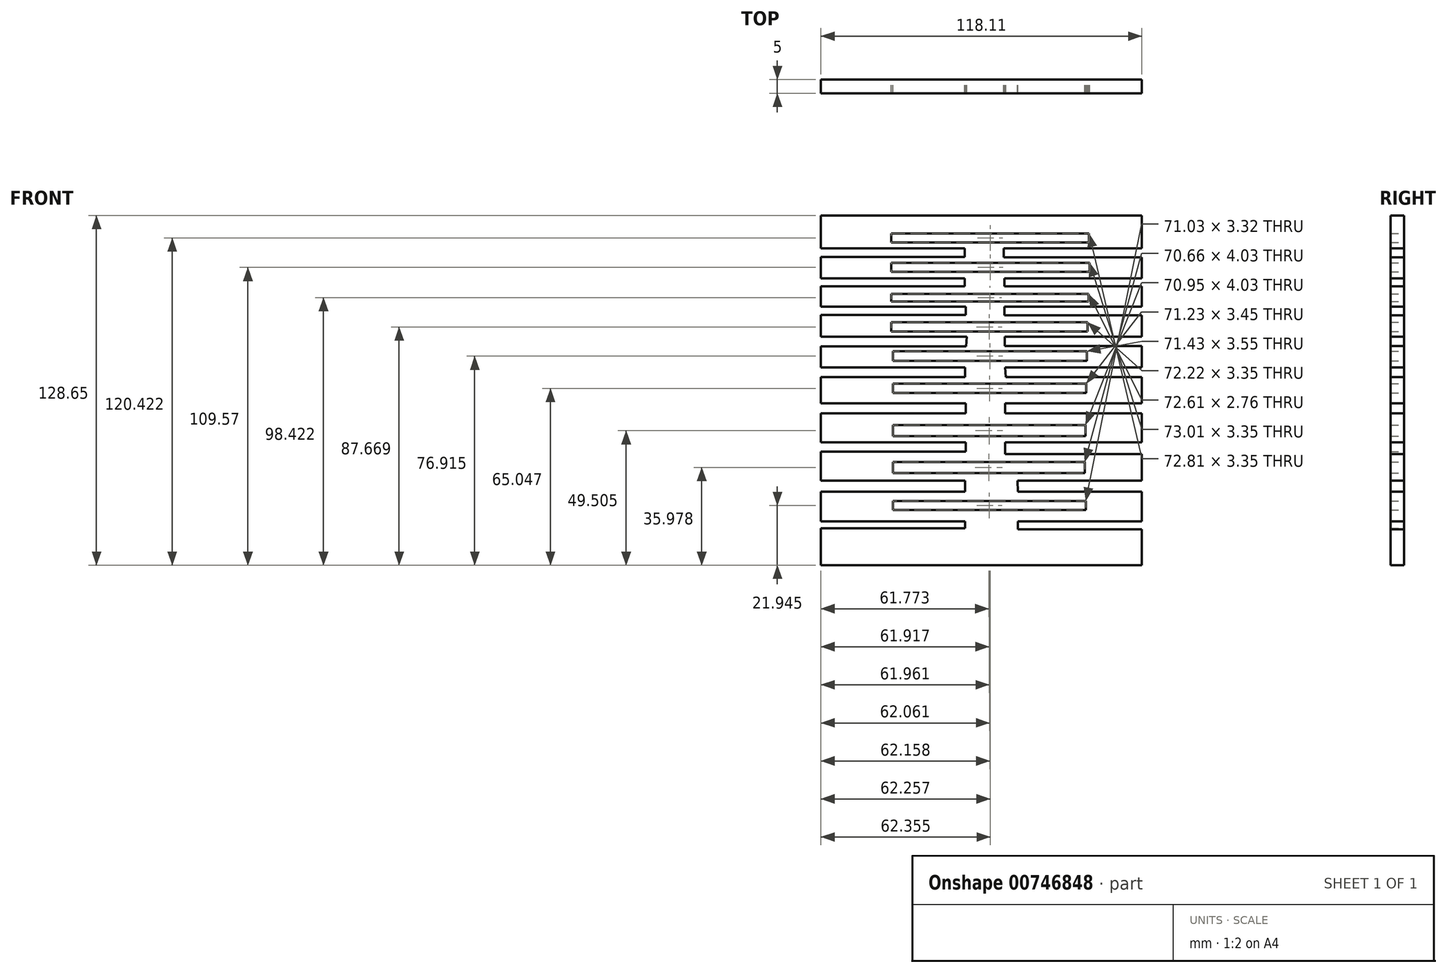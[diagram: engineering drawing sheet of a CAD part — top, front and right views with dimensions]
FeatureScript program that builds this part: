
annotation { "Feature Type Name" : "Feature", "Feature Type Description" : "" }
export const myFeature = defineFeature(function(context is Context, id is Id, definition is map)
    precondition{}
    {
        {
            var Q0;
            Q0=qCreatedBy(makeId("Front.planeOp"),FACE);
            var sketch = newSketch(context, id + "F0", { "sketchPlane" : qUnion([Q0])});
            skLineSegment(sketch, "E0.bottom", {"start": v(-61.27, 59.43) * mm, "end": v(56.84, 59.43) * mm});
            skLineSegment(sketch, "E0.top", {"start": v(-61.27, -69.22) * mm, "end": v(56.84, -69.22) * mm});
            skLineSegment(sketch, "E0.left", {"start": v(-61.27, 59.43) * mm, "end": v(-61.27, 47.35) * mm});
            skLineSegment(sketch, "E0.right", {"start": v(56.84, 59.43) * mm, "end": v(56.84, 47.35) * mm});
            skLineSegment(sketch, "E1.bottom", {"start": v(-34.83, -45.62) * mm, "end": v(36.2, -45.62) * mm});
            skLineSegment(sketch, "E1.top", {"start": v(-34.83, -48.93) * mm, "end": v(36.2, -48.93) * mm});
            skLineSegment(sketch, "E1.left", {"start": v(-34.83, -45.62) * mm, "end": v(-34.83, -48.93) * mm});
            skLineSegment(sketch, "E1.right", {"start": v(36.2, -45.62) * mm, "end": v(36.2, -48.93) * mm});
            skLineSegment(sketch, "E2.bottom", {"start": v(56.84, -38.13) * mm, "end": v(11.08, -38.13) * mm});
            skLineSegment(sketch, "E2.top", {"start": v(56.84, -42.16) * mm, "end": v(11.2, -42.16) * mm});
            skLineSegment(sketch, "E2.right", {"start": v(11.08, -38.13) * mm, "end": v(11.2, -42.16) * mm});
            skLineSegment(sketch, "E3.bottom", {"start": v(-61.27, -38.13) * mm, "end": v(-8.2, -38.13) * mm});
            skLineSegment(sketch, "E3.top", {"start": v(-61.27, -42.16) * mm, "end": v(-8.2, -42.16) * mm});
            skLineSegment(sketch, "E3.right", {"start": v(-8.2, -38.13) * mm, "end": v(-8.2, -42.16) * mm});
            skLineSegment(sketch, "E4.trimOffspring", {"start": v(-61.27, -42.16) * mm, "end": v(-61.27, -53.08) * mm});
            skLineSegment(sketch, "E5.trimOffspring", {"start": v(56.84, -42.16) * mm, "end": v(56.84, -53.08) * mm});
            skLineSegment(sketch, "E6.bottom", {"start": v(-34.83, -31.23) * mm, "end": v(35.83, -31.23) * mm});
            skLineSegment(sketch, "E6.top", {"start": v(-34.83, -35.26) * mm, "end": v(35.83, -35.26) * mm});
            skLineSegment(sketch, "E6.left", {"start": v(-34.83, -31.23) * mm, "end": v(-34.83, -35.26) * mm});
            skLineSegment(sketch, "E6.right", {"start": v(35.83, -31.23) * mm, "end": v(35.83, -35.26) * mm});
            skLineSegment(sketch, "E7.bottom", {"start": v(56.84, -24.03) * mm, "end": v(6.48, -24.03) * mm});
            skLineSegment(sketch, "E7.top", {"start": v(56.84, -28.35) * mm, "end": v(6.48, -28.35) * mm});
            skLineSegment(sketch, "E7.right", {"start": v(6.48, -24.03) * mm, "end": v(6.48, -28.35) * mm});
            skLineSegment(sketch, "E8.bottom", {"start": v(-61.27, -24.03) * mm, "end": v(-7.91, -24.03) * mm});
            skLineSegment(sketch, "E8.top", {"start": v(-61.27, -27.49) * mm, "end": v(-7.91, -27.49) * mm});
            skLineSegment(sketch, "E8.right", {"start": v(-7.91, -24.03) * mm, "end": v(-7.91, -27.49) * mm});
            skLineSegment(sketch, "E9.bottom", {"start": v(-34.83, -17.7) * mm, "end": v(36.12, -17.7) * mm});
            skLineSegment(sketch, "E9.top", {"start": v(-34.83, -21.73) * mm, "end": v(36.12, -21.73) * mm});
            skLineSegment(sketch, "E9.left", {"start": v(-34.83, -17.7) * mm, "end": v(-34.83, -21.73) * mm});
            skLineSegment(sketch, "E9.right", {"start": v(36.12, -17.7) * mm, "end": v(36.12, -21.73) * mm});
            skLineSegment(sketch, "E10.bottom", {"start": v(-7.91, -9.64) * mm, "end": v(-61.27, -9.64) * mm});
            skLineSegment(sketch, "E10.top", {"start": v(-7.91, -13.38) * mm, "end": v(-61.27, -13.38) * mm});
            skLineSegment(sketch, "E10.left", {"start": v(-7.91, -9.64) * mm, "end": v(-7.91, -13.38) * mm});
            skLineSegment(sketch, "E11.bottom", {"start": v(6.48, -9.64) * mm, "end": v(56.84, -9.64) * mm});
            skLineSegment(sketch, "E11.top", {"start": v(6.48, -13.38) * mm, "end": v(56.84, -13.38) * mm});
            skLineSegment(sketch, "E11.left", {"start": v(6.48, -9.64) * mm, "end": v(6.48, -13.38) * mm});
            skLineSegment(sketch, "E12.trimOffspring", {"start": v(-61.27, -13.38) * mm, "end": v(-61.27, -24.03) * mm});
            skLineSegment(sketch, "E13.trimOffspring", {"start": v(56.84, -13.38) * mm, "end": v(56.84, -24.03) * mm});
            skLineSegment(sketch, "E14.bottom", {"start": v(-34.83, -2.45) * mm, "end": v(36.4, -2.45) * mm});
            skLineSegment(sketch, "E14.top", {"start": v(-34.83, -5.9) * mm, "end": v(36.4, -5.9) * mm});
            skLineSegment(sketch, "E14.left", {"start": v(-34.83, -2.45) * mm, "end": v(-34.83, -5.9) * mm});
            skLineSegment(sketch, "E14.right", {"start": v(36.4, -2.45) * mm, "end": v(36.4, -5.9) * mm});
            skLineSegment(sketch, "E15.bottom", {"start": v(-61.27, 3.6) * mm, "end": v(-8.2, 3.6) * mm});
            skLineSegment(sketch, "E15.top", {"start": v(-61.27, 0) * mm, "end": v(-8.2, 0) * mm});
            skLineSegment(sketch, "E15.right", {"start": v(-8.2, 3.6) * mm, "end": v(-8.2, 0) * mm});
            skLineSegment(sketch, "E16.trimOffspring", {"start": v(-61.27, 0) * mm, "end": v(-61.27, -9.64) * mm});
            skLineSegment(sketch, "E17.bottom", {"start": v(56.84, 3.6) * mm, "end": v(6.48, 3.6) * mm});
            skLineSegment(sketch, "E17.top", {"start": v(56.84, 0) * mm, "end": v(6.76, 0) * mm});
            skLineSegment(sketch, "E17.right", {"start": v(6.48, 3.6) * mm, "end": v(6.76, 0) * mm});
            skLineSegment(sketch, "E18.trimOffspring", {"start": v(56.84, 0) * mm, "end": v(56.84, -9.64) * mm});
            skLineSegment(sketch, "E19.trimOffspring", {"start": v(56.84, -28.35) * mm, "end": v(56.84, -38.13) * mm});
            skLineSegment(sketch, "E20.trimOffspring", {"start": v(-61.27, -27.49) * mm, "end": v(-61.27, -38.13) * mm});
            skLineSegment(sketch, "E21.bottom", {"start": v(-34.83, 9.47) * mm, "end": v(36.6, 9.47) * mm});
            skLineSegment(sketch, "E21.top", {"start": v(-34.83, 5.92) * mm, "end": v(36.6, 5.92) * mm});
            skLineSegment(sketch, "E21.left", {"start": v(-34.83, 9.47) * mm, "end": v(-34.83, 5.92) * mm});
            skLineSegment(sketch, "E21.right", {"start": v(36.6, 9.47) * mm, "end": v(36.6, 5.92) * mm});
            skLineSegment(sketch, "E22.bottom", {"start": v(-61.27, 14.8) * mm, "end": v(-7.6, 14.8) * mm});
            skLineSegment(sketch, "E22.top", {"start": v(-61.27, 11.25) * mm, "end": v(-7.8, 11.25) * mm});
            skLineSegment(sketch, "E22.right", {"start": v(-7.6, 14.8) * mm, "end": v(-7.8, 11.25) * mm});
            skLineSegment(sketch, "E23.trimOffspring", {"start": v(-61.27, 11.25) * mm, "end": v(-61.27, 3.6) * mm});
            skLineSegment(sketch, "E24.bottom", {"start": v(56.84, 14.8) * mm, "end": v(6.41, 14.8) * mm});
            skLineSegment(sketch, "E24.top", {"start": v(56.84, 11.44) * mm, "end": v(6.41, 11.44) * mm});
            skLineSegment(sketch, "E24.right", {"start": v(6.41, 14.8) * mm, "end": v(6.41, 11.44) * mm});
            skLineSegment(sketch, "E25.trimOffspring", {"start": v(56.84, 11.44) * mm, "end": v(56.84, 3.6) * mm});
            skLineSegment(sketch, "E26.bottom", {"start": v(-35.42, 20.13) * mm, "end": v(36.8, 20.13) * mm});
            skLineSegment(sketch, "E26.top", {"start": v(-35.42, 16.77) * mm, "end": v(36.8, 16.77) * mm});
            skLineSegment(sketch, "E26.left", {"start": v(-35.42, 20.13) * mm, "end": v(-35.42, 16.77) * mm});
            skLineSegment(sketch, "E26.right", {"start": v(36.8, 20.13) * mm, "end": v(36.8, 16.77) * mm});
            skLineSegment(sketch, "E27.bottom", {"start": v(-61.27, 25.85) * mm, "end": v(-8, 25.85) * mm});
            skLineSegment(sketch, "E27.top", {"start": v(-61.27, 22.89) * mm, "end": v(-8, 22.89) * mm});
            skLineSegment(sketch, "E27.right", {"start": v(-8, 25.85) * mm, "end": v(-8, 22.89) * mm});
            skLineSegment(sketch, "E28.trimOffspring", {"start": v(-61.27, 22.89) * mm, "end": v(-61.27, 14.8) * mm});
            skLineSegment(sketch, "E29.bottom", {"start": v(56.84, 25.85) * mm, "end": v(6.22, 25.85) * mm});
            skLineSegment(sketch, "E29.top", {"start": v(56.84, 22.7) * mm, "end": v(6.22, 22.7) * mm});
            skLineSegment(sketch, "E29.right", {"start": v(6.22, 25.85) * mm, "end": v(6.22, 22.7) * mm});
            skLineSegment(sketch, "E30.trimOffspring", {"start": v(56.84, 22.7) * mm, "end": v(56.84, 14.8) * mm});
            skLineSegment(sketch, "E31.bottom", {"start": v(-35.42, 30.58) * mm, "end": v(37.2, 30.58) * mm});
            skLineSegment(sketch, "E31.top", {"start": v(-35.42, 27.82) * mm, "end": v(37.2, 27.82) * mm});
            skLineSegment(sketch, "E31.left", {"start": v(-35.42, 30.58) * mm, "end": v(-35.42, 27.82) * mm});
            skLineSegment(sketch, "E31.right", {"start": v(37.2, 30.58) * mm, "end": v(37.2, 27.82) * mm});
            skLineSegment(sketch, "E32.bottom", {"start": v(-61.27, 36.3) * mm, "end": v(-8.39, 36.3) * mm});
            skLineSegment(sketch, "E32.top", {"start": v(-61.27, 33.35) * mm, "end": v(-8.39, 33.35) * mm});
            skLineSegment(sketch, "E32.right", {"start": v(-8.39, 36.3) * mm, "end": v(-8.39, 33.35) * mm});
            skLineSegment(sketch, "E33.trimOffspring", {"start": v(-61.27, 33.35) * mm, "end": v(-61.27, 25.85) * mm});
            skLineSegment(sketch, "E34.bottom", {"start": v(56.84, 36.3) * mm, "end": v(6.22, 36.3) * mm});
            skLineSegment(sketch, "E34.top", {"start": v(56.84, 33.35) * mm, "end": v(6.22, 33.35) * mm});
            skLineSegment(sketch, "E34.right", {"start": v(6.22, 36.3) * mm, "end": v(6.22, 33.35) * mm});
            skLineSegment(sketch, "E35.trimOffspring", {"start": v(56.84, 33.35) * mm, "end": v(56.84, 25.85) * mm});
            skLineSegment(sketch, "E36.bottom", {"start": v(-35.42, 42.03) * mm, "end": v(37.59, 42.03) * mm});
            skLineSegment(sketch, "E36.top", {"start": v(-35.42, 38.67) * mm, "end": v(37.59, 38.67) * mm});
            skLineSegment(sketch, "E36.left", {"start": v(-35.42, 42.03) * mm, "end": v(-35.42, 38.67) * mm});
            skLineSegment(sketch, "E36.right", {"start": v(37.59, 42.03) * mm, "end": v(37.59, 38.67) * mm});
            skLineSegment(sketch, "E37.bottom", {"start": v(-61.27, 47.35) * mm, "end": v(-8.39, 47.35) * mm});
            skLineSegment(sketch, "E37.top", {"start": v(-61.27, 44.2) * mm, "end": v(-8.39, 44.2) * mm});
            skLineSegment(sketch, "E37.right", {"start": v(-8.39, 47.35) * mm, "end": v(-8.39, 44.2) * mm});
            skLineSegment(sketch, "E38.trimOffspring", {"start": v(-61.27, 44.2) * mm, "end": v(-61.27, 36.3) * mm});
            skLineSegment(sketch, "E39.bottom", {"start": v(56.84, 47.35) * mm, "end": v(6.02, 47.35) * mm});
            skLineSegment(sketch, "E39.top", {"start": v(56.84, 44) * mm, "end": v(6.02, 44) * mm});
            skLineSegment(sketch, "E39.right", {"start": v(6.02, 47.35) * mm, "end": v(6.02, 44) * mm});
            skLineSegment(sketch, "E40.trimOffspring", {"start": v(56.84, 44) * mm, "end": v(56.84, 36.3) * mm});
            skLineSegment(sketch, "E41.bottom", {"start": v(-35.42, 52.88) * mm, "end": v(37.4, 52.88) * mm});
            skLineSegment(sketch, "E41.top", {"start": v(-35.42, 49.53) * mm, "end": v(37.4, 49.53) * mm});
            skLineSegment(sketch, "E41.left", {"start": v(-35.42, 52.88) * mm, "end": v(-35.42, 49.53) * mm});
            skLineSegment(sketch, "E41.right", {"start": v(37.4, 52.88) * mm, "end": v(37.4, 49.53) * mm});
            skLineSegment(sketch, "E42.bottom", {"start": v(-8.2, -53.08) * mm, "end": v(-61.27, -53.08) * mm});
            skLineSegment(sketch, "E42.top", {"start": v(-8.2, -55.7) * mm, "end": v(-61.27, -55.7) * mm});
            skLineSegment(sketch, "E42.left", {"start": v(-8.2, -53.08) * mm, "end": v(-8.2, -55.7) * mm});
            skLineSegment(sketch, "E43.bottom", {"start": v(56.84, -53.08) * mm, "end": v(11.2, -53.08) * mm});
            skLineSegment(sketch, "E43.top", {"start": v(56.84, -56.04) * mm, "end": v(11.2, -56.04) * mm});
            skLineSegment(sketch, "E43.right", {"start": v(11.2, -53.08) * mm, "end": v(11.2, -56.04) * mm});
            skLineSegment(sketch, "E44.trimOffspring", {"start": v(-61.27, -55.7) * mm, "end": v(-61.27, -69.22) * mm});
            skLineSegment(sketch, "E45.trimOffspring", {"start": v(56.84, -56.04) * mm, "end": v(56.84, -69.22) * mm});
            skSolve(sketch);
        }
        {
            var Q0;
            Q0=makeQuery(id+"F0.imprint","IMPRINT",FACE,{"disambiguationData":[TD([[makeQuery(id+"F0.imprint","IMPRINT",EDGE,{"derivedFrom":sQuery(id+"F0.wireOp",EDGE,"E0.bottom")}),-1.0]])]});
            extrude(context, id + "F1", {"entities" : qUnion([Q0]), "depth" : 5 * mm, "offsetDistance" : 25.4 * mm});
        }
    });
